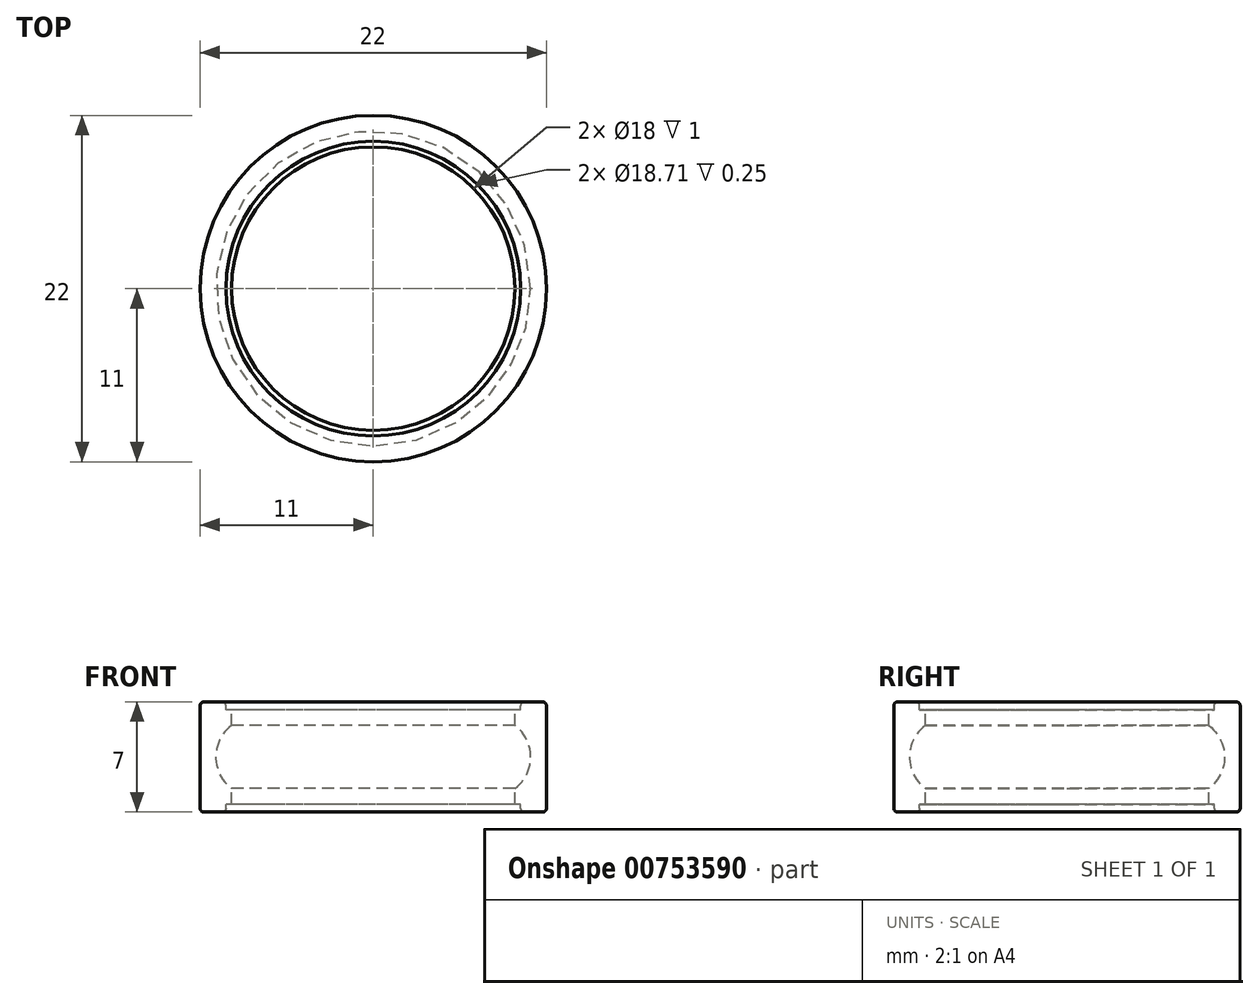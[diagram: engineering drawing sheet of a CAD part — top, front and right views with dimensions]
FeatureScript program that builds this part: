
annotation { "Feature Type Name" : "Feature", "Feature Type Description" : "" }
export const myFeature = defineFeature(function(context is Context, id is Id, definition is map)
    precondition{}
    {
        {
            var Q0;
            Q0=qCreatedBy(makeId("Front.planeOp"),FACE);
            var sketch = newSketch(context, id + "F0", { "sketchPlane" : qUnion([Q0])});
            skLineSegment(sketch, "E0", {"start": v(0, 2.1) * mm, "end": v(0, -2.2) * mm});
            skLineSegment(sketch, "E1", {"start": v(9, 0) * mm, "end": v(11, 0) * mm});
            skLineSegment(sketch, "E2", {"start": v(11, 0) * mm, "end": v(11, 3.25) * mm});
            skLineSegment(sketch, "E3", {"start": v(11, 0) * mm, "end": v(11, -3.25) * mm});
            skLineSegment(sketch, "E4", {"start": v(10.75, -3.5) * mm, "end": v(9.6, -3.5) * mm});
            skLineSegment(sketch, "E5", {"start": v(10.75, 3.5) * mm, "end": v(9.6, 3.5) * mm});
            skArc(sketch, "E6", {"start": v(9, -2) * mm, "mid": v(10, 0) * mm, "end": v(9, 2) * mm});
            skLineSegment(sketch, "E7", {"start": v(9, 3) * mm, "end": v(9, 2) * mm});
            skPoint(sketch, "E8.visualSharp", {"position": v(11, 3.5) * mm});
            skArc(sketch, "E8.filletArc", {"start": v(11, 3.25) * mm, "mid": v(10.93, 3.43) * mm, "end": v(10.75, 3.5) * mm});
            skPoint(sketch, "E9.visualSharp", {"position": v(11, -3.5) * mm});
            skArc(sketch, "E9.filletArc", {"start": v(10.75, -3.5) * mm, "mid": v(10.93, -3.43) * mm, "end": v(11, -3.25) * mm});
            skPoint(sketch, "E10.visualSharp", {"position": v(9, -3.5) * mm});
            skPoint(sketch, "E11.visualSharp", {"position": v(9, 3.5) * mm});
            skPoint(sketch, "E12.end.orphan", {"position": v(4, 0) * mm});
            skLineSegment(sketch, "E13.trimOffspring", {"start": v(9, -2) * mm, "end": v(9, -3) * mm});
            skLineSegment(sketch, "E14", {"start": v(9.36, 3.25) * mm, "end": v(9.36, 3) * mm});
            skLineSegment(sketch, "E15", {"start": v(9, -3) * mm, "end": v(9.36, -3) * mm});
            skLineSegment(sketch, "E16", {"start": v(9, 3) * mm, "end": v(9.36, 3) * mm});
            skLineSegment(sketch, "E17.trimOffspring", {"start": v(9.36, -3) * mm, "end": v(9.36, -3.25) * mm});
            skPoint(sketch, "E18.visualSharp", {"position": v(9.36, 3.5) * mm});
            skArc(sketch, "E18.filletArc", {"start": v(9.6, 3.5) * mm, "mid": v(9.43, 3.43) * mm, "end": v(9.36, 3.25) * mm});
            skPoint(sketch, "E19.visualSharp", {"position": v(9.36, -3.5) * mm});
            skArc(sketch, "E19.filletArc", {"start": v(9.36, -3.25) * mm, "mid": v(9.43, -3.43) * mm, "end": v(9.6, -3.5) * mm});
            skSolve(sketch);
        }
        {
            var Q0;
            Q0 = qSketchRegion(id + "F0", true);
            var Q1;
            Q1=sQuery(id+"F0.wireOp",EDGE,"E0");
            revolve(context, id + "F1", {"surfaceOperationType" : NewSurfaceOperationType.NEW, "entities" : qUnion([Q0]), "axis" : qUnion([Q1]), "revolveType" : RevolveType.FULL});
        }
    });
